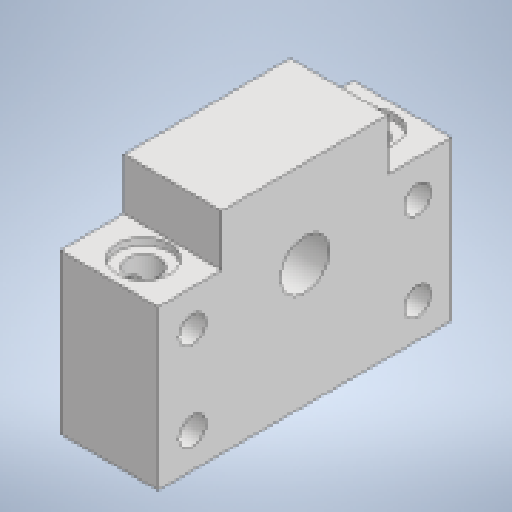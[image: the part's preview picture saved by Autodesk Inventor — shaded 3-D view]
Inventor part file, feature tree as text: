
AUTODESK INVENTOR PART (.ipt)
format: ipt  version: 2023 (Build 270158000, 158)  size: 194,560 bytes
history: native  units: mm
features: extrude x4, sketch x4
ambient origin geometry x8: Origin, YZ Plane, XZ Plane, XY Plane, X Axis, Y Axis, Z Axis, Center Point
bodies: Solid1 (feature_tree)
feature tree (8):
  extrude  "Extrusion1"  Depth=60.0mm
  extrude  "Extrusion2"  Depth=32.5mm
  extrude  "Extrusion3"  Depth=25.0mm
  extrude  "Extrusion4"  Depth=10.0mm
  sketch  "Sketch1"  dims[d0=34.0mm d1=60.0mm]
  sketch  "Sketch2"  dims[d2=43.0mm d3=32.5mm]
  sketch  "Sketch3"  dims[d4=5.5mm d6=25.0mm]
  sketch  "Sketch4"  dims[d7=18.0mm d8=46.0mm d9=10.0mm d10=20.0mm d11=0.0mm d12=10.8mm d13=10.8mm d14=46.0mm d15=7.0mm d16=10.0mm d17=1.5mm d18=0.0mm d19=6.6mm d20=5.0mm d21=0.0mm d22=22.0mm d23=10.0mm d24=0.0mm]
